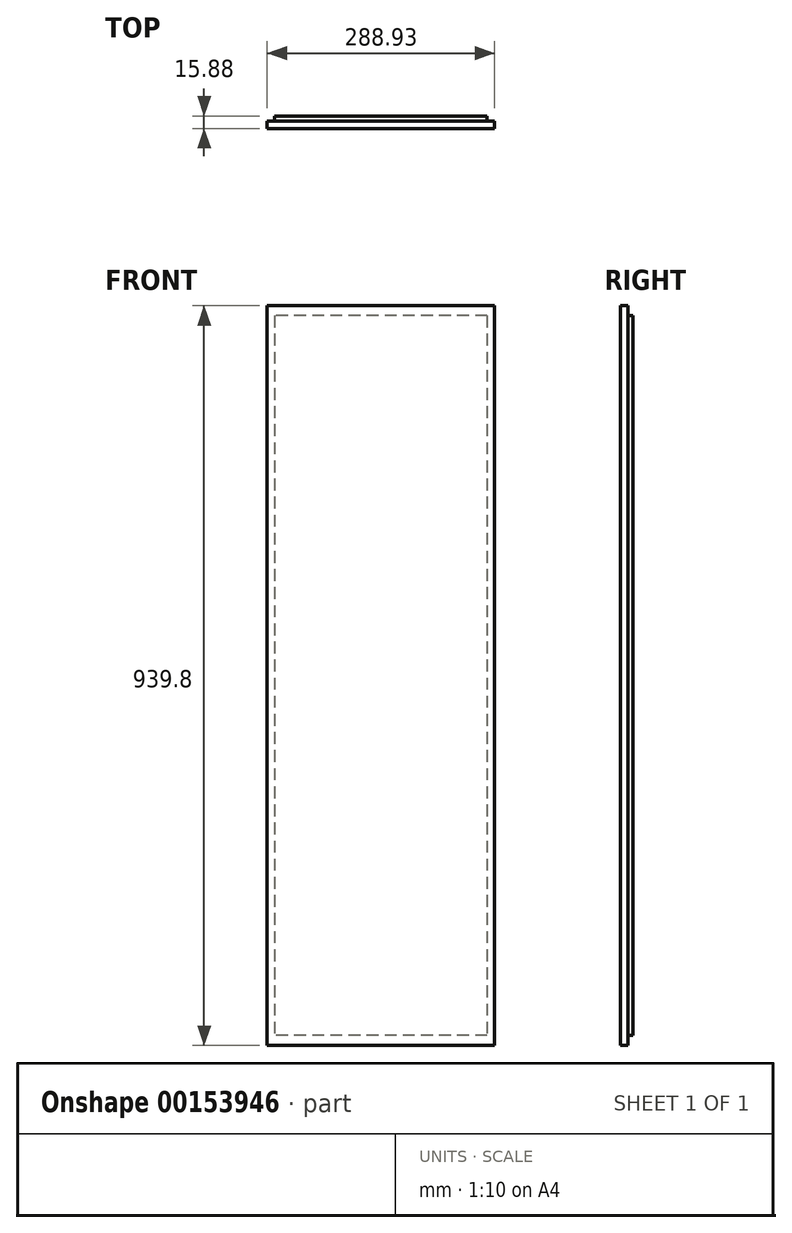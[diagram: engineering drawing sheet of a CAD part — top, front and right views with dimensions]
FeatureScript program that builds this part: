
annotation { "Feature Type Name" : "Feature", "Feature Type Description" : "" }
export const myFeature = defineFeature(function(context is Context, id is Id, definition is map)
    precondition{}
    {
        {
            var Q0;
            Q0=qCreatedBy(makeId("Front.planeOp"),FACE);
            var sketch = newSketch(context, id + "F0", { "sketchPlane" : qUnion([Q0])});
            skLineSegment(sketch, "E0.bottom", {"start": v(0, 0) * mm, "end": v(288.93, 0) * mm});
            skLineSegment(sketch, "E0.top", {"start": v(0, 939.8) * mm, "end": v(288.92, 939.8) * mm});
            skLineSegment(sketch, "E0.left", {"start": v(0, 0) * mm, "end": v(0, 939.8) * mm});
            skLineSegment(sketch, "E0.right", {"start": v(288.93, 0) * mm, "end": v(288.92, 939.8) * mm});
            skSolve(sketch);
        }
        {
            var Q0;
            Q0=makeQuery(id+"F0.imprint","IMPRINT",FACE,{"disambiguationData":[TD([[makeQuery(id+"F0.imprint","IMPRINT",EDGE,{"derivedFrom":sQuery(id+"F0.wireOp",EDGE,"E0.bottom")}),1.0]])]});
            extrude(context, id + "F1", {"entities" : qUnion([Q0]), "depth" : 9.52 * mm, "offsetDistance" : 25.4 * mm});
        }
        {
            var Q0;
            Q0=makeQuery(id+"F1.opExtrude","CAP_FACE",FACE,{"disambiguationData":[OSD([sQuery(id+"F0.wireOp",EDGE,"E0.bottom"),sQuery(id+"F0.wireOp",EDGE,"E0.top"),sQuery(id+"F0.wireOp",EDGE,"E0.left"),sQuery(id+"F0.wireOp",EDGE,"E0.right")])],"isStart":true});
            var sketch = newSketch(context, id + "F2", { "sketchPlane" : qUnion([Q0])});
            skLineSegment(sketch, "E1.bottom", {"start": v(-279.4, 927.1) * mm, "end": v(-9.53, 927.1) * mm});
            skLineSegment(sketch, "E1.top", {"start": v(-279.4, 12.7) * mm, "end": v(-9.52, 12.7) * mm});
            skLineSegment(sketch, "E1.left", {"start": v(-279.4, 927.1) * mm, "end": v(-279.4, 12.7) * mm});
            skLineSegment(sketch, "E1.right", {"start": v(-9.53, 927.1) * mm, "end": v(-9.52, 12.7) * mm});
            skSolve(sketch);
        }
        {
            var Q0;
            Q0=makeQuery(id+"F2.imprint","IMPRINT",FACE,{"disambiguationData":[TD([[makeQuery(id+"F2.imprint","IMPRINT",EDGE,{"derivedFrom":sQuery(id+"F2.wireOp",EDGE,"E1.bottom")}),-1.0]])]});
            extrude(context, id + "F3", {"entities" : qUnion([Q0]), "operationType" : NewBodyOperationType.ADD, "depth" : 6.35 * mm});
        }
    });
